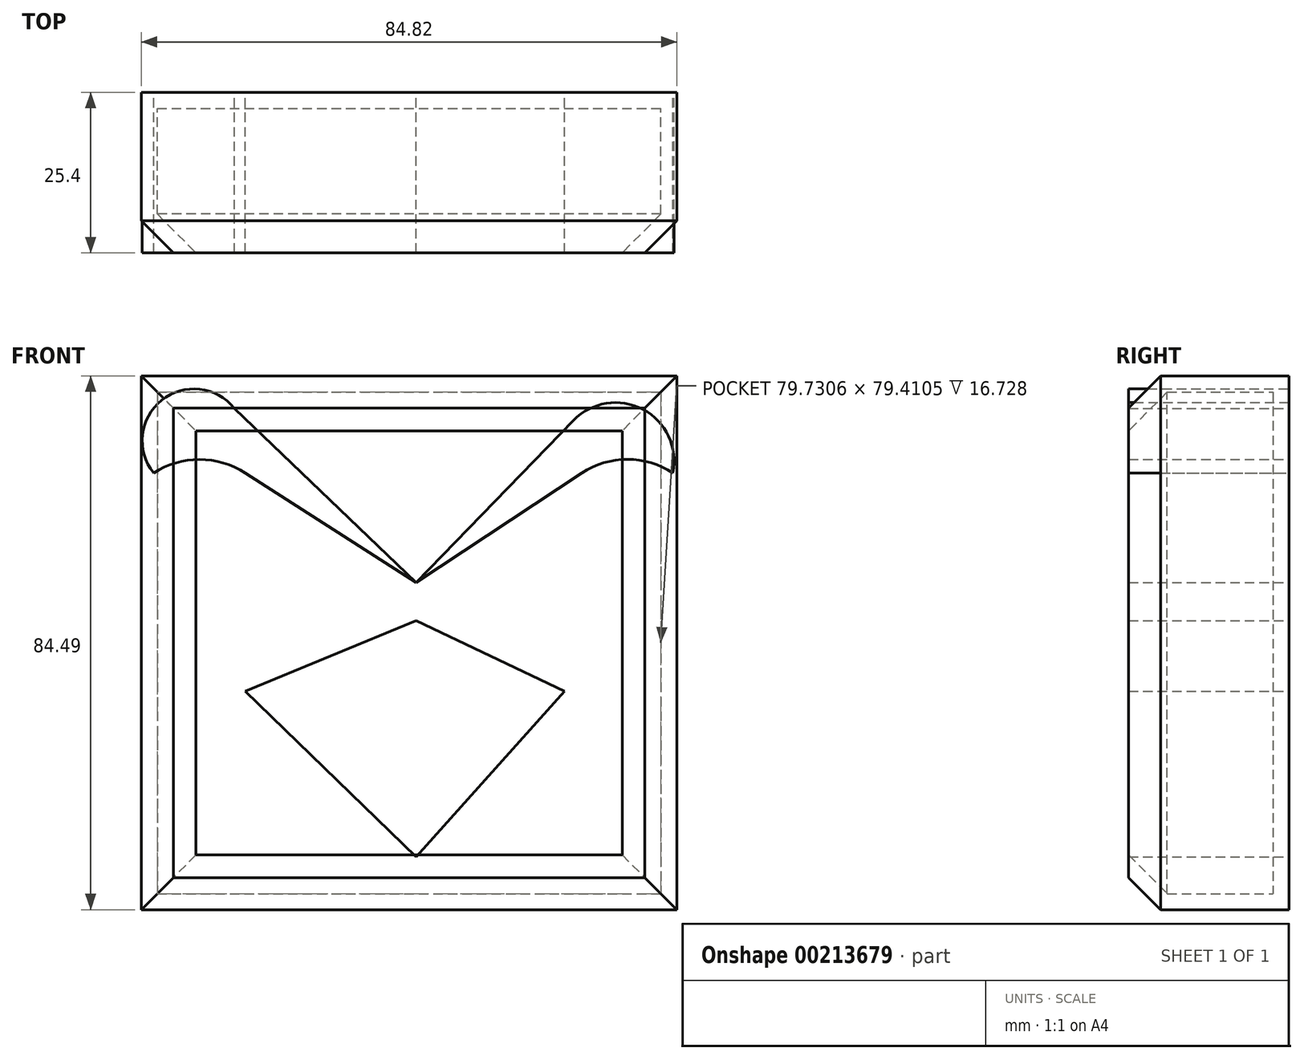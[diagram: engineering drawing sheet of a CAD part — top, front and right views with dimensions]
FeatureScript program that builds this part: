
annotation { "Feature Type Name" : "Feature", "Feature Type Description" : "" }
export const myFeature = defineFeature(function(context is Context, id is Id, definition is map)
    precondition{}
    {
        {
            var Q0;
            Q0=qCreatedBy(makeId("Front.planeOp"),FACE);
            var sketch = newSketch(context, id + "F0", { "sketchPlane" : qUnion([Q0])});
            skLineSegment(sketch, "E0", {"start": v(-28.77, 44.8) * mm, "end": v(0, 17.2) * mm});
            skLineSegment(sketch, "E1", {"start": v(0, 17.2) * mm, "end": v(24.9, 42.89) * mm});
            skPoint(sketch, "E2.end.orphan", {"position": v(-35.18, 0) * mm});
            skLineSegment(sketch, "E3", {"start": v(0, 17.2) * mm, "end": v(-35.18, 0) * mm});
            skLineSegment(sketch, "E4", {"start": v(-0.68, 17.2) * mm, "end": v(35.43, 0) * mm});
            skLineSegment(sketch, "E5", {"start": v(-35.18, 0) * mm, "end": v(0, -34.1) * mm});
            skLineSegment(sketch, "E6", {"start": v(35.52, 0) * mm, "end": v(0, -34.1) * mm});
            skArc(sketch, "E7", {"start": v(-28.77, 44.8) * mm, "mid": v(-40.29, 46.08) * mm, "end": v(-41.56, 34.56) * mm});
            skPoint(sketch, "E8.orphan", {"position": v(32, 34.56) * mm});
            skPoint(sketch, "E9.orphan", {"position": v(24.9, 34.56) * mm});
            skPoint(sketch, "E10.end.orphan", {"position": v(32, 37.76) * mm});
            skPoint(sketch, "E11.endSnap0", {"position": v(-14.38, 31) * mm});
            skPoint(sketch, "E11.end.orphan", {"position": v(26.24, 31) * mm});
            skArc(sketch, "E12", {"start": v(40.65, 34.56) * mm, "mid": v(35.9, 44.63) * mm, "end": v(24.9, 42.89) * mm});
            skLineSegment(sketch, "E13", {"start": v(0, 11.2) * mm, "end": v(-27.04, 0) * mm});
            skLineSegment(sketch, "E14", {"start": v(0, 11.2) * mm, "end": v(23.52, 0) * mm});
            skLineSegment(sketch, "E15", {"start": v(-27.04, 0) * mm, "end": v(0, -26.2) * mm});
            skLineSegment(sketch, "E16", {"start": v(23.52, 0) * mm, "end": v(0, -26.2) * mm});
            skLineSegment(sketch, "E17", {"start": v(0, 17.2) * mm, "end": v(26.24, 34.56) * mm});
            skLineSegment(sketch, "E18", {"start": v(0, 17.2) * mm, "end": v(-27.04, 34.56) * mm});
            skArc(sketch, "E19", {"start": v(-27.04, 34.56) * mm, "mid": v(-34.3, 36.7) * mm, "end": v(-41.56, 34.56) * mm});
            skArc(sketch, "E20", {"start": v(40.65, 34.56) * mm, "mid": v(33.44, 36.73) * mm, "end": v(26.24, 34.56) * mm});
            skSolve(sketch);
        }
        {
            var Q0;
            Q0=qCreatedBy(makeId("Front.planeOp"),FACE);
            var sketch = newSketch(context, id + "F1", { "sketchPlane" : qUnion([Q0])});
            skLineSegment(sketch, "E21.bottom", {"start": v(-43.53, 49.92) * mm, "end": v(41.29, 49.92) * mm});
            skLineSegment(sketch, "E21.top", {"start": v(-43.53, -34.57) * mm, "end": v(41.29, -34.57) * mm});
            skLineSegment(sketch, "E21.left", {"start": v(-43.53, 49.92) * mm, "end": v(-43.53, -34.57) * mm});
            skLineSegment(sketch, "E21.right", {"start": v(41.29, 49.92) * mm, "end": v(41.29, -34.57) * mm});
            skSolve(sketch);
        }
        {
            var Q0;
            Q0=makeQuery(id+"F0.imprint","IMPRINT",FACE,{"disambiguationData":[TD([[makeQuery(id+"F0.imprint","IMPRINT",EDGE,{"derivedFrom":sQuery(id+"F0.wireOp",EDGE,"E13")}),1.0]])]});
            var Q1;
            Q1=makeQuery(id+"F0.imprint","IMPRINT",FACE,{"disambiguationData":[TD([[makeQuery(id+"F0.imprint","IMPRINT",EDGE,{"derivedFrom":sQuery(id+"F0.wireOp",EDGE,"E0")}),-1.0]])]});
            var Q2;
            Q2=makeQuery(id+"F0.imprint","IMPRINT",FACE,{"disambiguationData":[TD([[makeQuery(id+"F0.imprint","IMPRINT",EDGE,{"derivedFrom":sQuery(id+"F0.wireOp",EDGE,"E1")}),-1.0]])]});
            var Q3;
            Q3=makeQuery(id+"F1.imprint","IMPRINT",FACE,{"disambiguationData":[TD([[makeQuery(id+"F1.imprint","IMPRINT",EDGE,{"derivedFrom":sQuery(id+"F1.wireOp",EDGE,"E21.bottom")}),-1.0]])]});
            extrude(context, id + "F2", {"entities" : qUnion([Q0, Q1, Q2, Q3]), "depth" : 25.4 * mm});
        }
        {
            var Q0;
            Q0=makeQuery(id+"F2.opExtrude","CAP_EDGE",EDGE,{"disambiguationData":[OSD([sQuery(id+"F1.wireOp",EDGE,"E21.left")])],"isStart":false});
            var Q1;
            Q1=makeQuery(id+"F2.opExtrude","CAP_EDGE",EDGE,{"disambiguationData":[OSD([sQuery(id+"F1.wireOp",EDGE,"E21.bottom")])],"isStart":false});
            var Q2;
            Q2=makeQuery(id+"F2.opExtrude","CAP_EDGE",EDGE,{"disambiguationData":[OSD([sQuery(id+"F1.wireOp",EDGE,"E21.right")])],"isStart":false});
            var Q3;
            Q3=makeQuery(id+"F2.opExtrude","CAP_EDGE",EDGE,{"disambiguationData":[OSD([sQuery(id+"F1.wireOp",EDGE,"E21.top")])],"isStart":false});
            chamfer(context, id + "F3", {"entities" : qUnion([Q0, Q1, Q2, Q3]), "width" : 5.08 * mm, "tangentPropagation" : true});
        }
        {
            var Q0;
            Q0=makeQuery(id+"F2.opExtrude","CAP_FACE",FACE,{"disambiguationData":[OSD([sQuery(id+"F1.wireOp",EDGE,"E21.bottom"),sQuery(id+"F1.wireOp",EDGE,"E21.top"),sQuery(id+"F1.wireOp",EDGE,"E21.left"),sQuery(id+"F1.wireOp",EDGE,"E21.right")])],"isStart":false});
            shell(context, id + "F4", {"entities" : qUnion([Q0]), "thickness" : 2.54 * mm});
        }
    });
